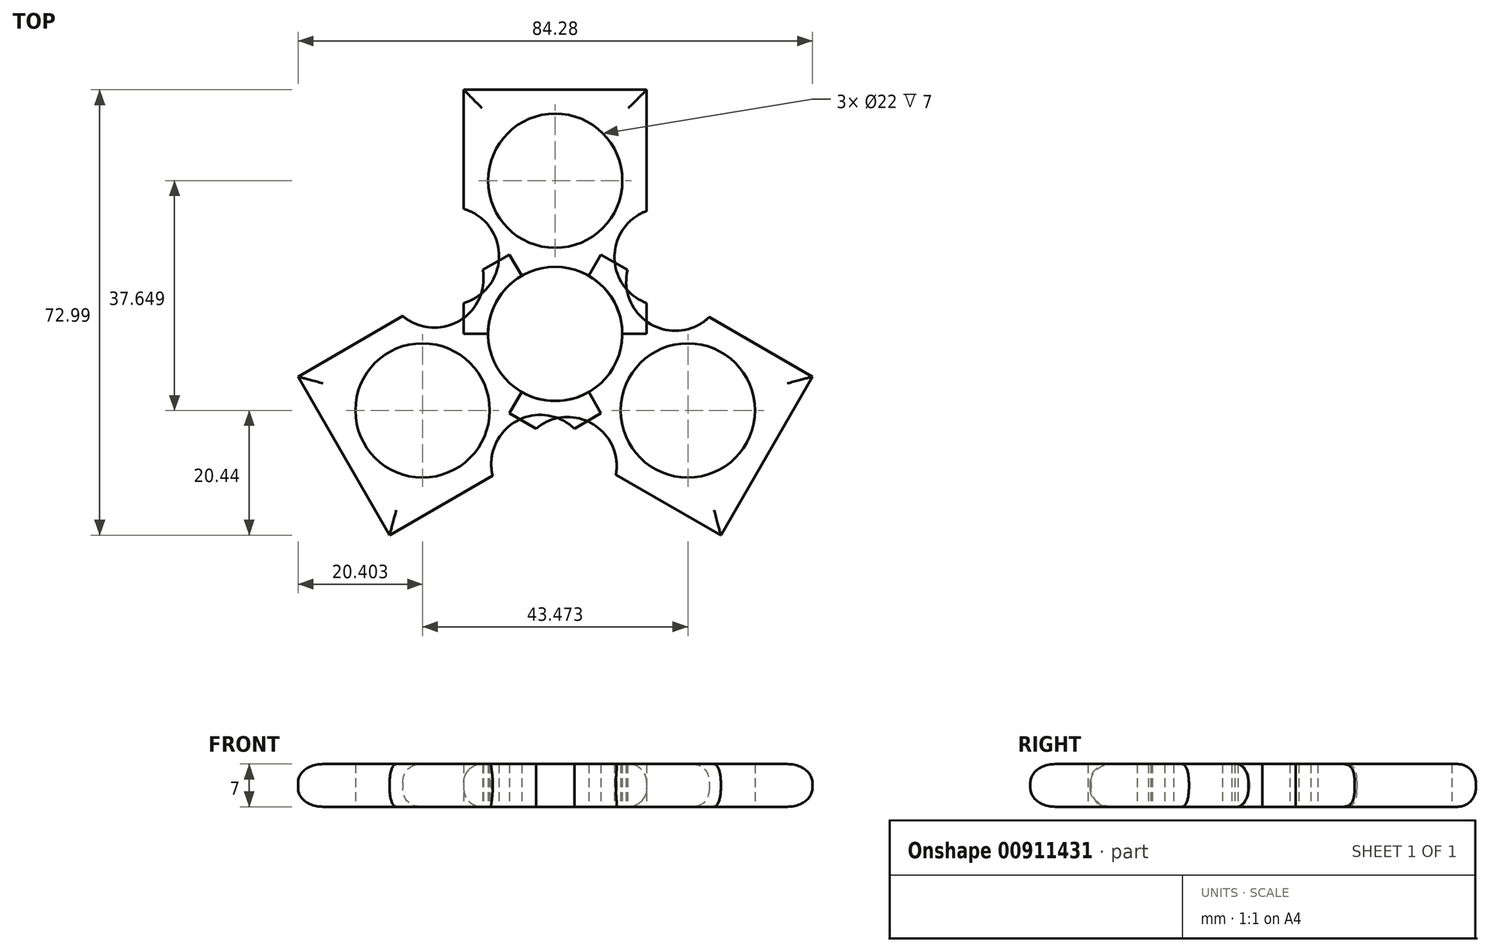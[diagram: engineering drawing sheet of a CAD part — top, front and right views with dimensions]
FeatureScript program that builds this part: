
annotation { "Feature Type Name" : "Feature", "Feature Type Description" : "" }
export const myFeature = defineFeature(function(context is Context, id is Id, definition is map)
    precondition{}
    {
        {
            var Q0;
            Q0=qCreatedBy(makeId("Top.planeOp"),FACE);
            var sketch = newSketch(context, id + "F0", { "sketchPlane" : qUnion([Q0])});
            skCircle(sketch, "E0", {"center": v(0, 0) * mm, "radius": 11 * mm});
            skLineSegment(sketch, "E1.bottom", {"start": v(0, 0) * mm, "end": v(15, 0) * mm});
            skLineSegment(sketch, "E1.top", {"start": v(0, 40) * mm, "end": v(15, 40) * mm});
            skLineSegment(sketch, "E1.left", {"start": v(0, 0) * mm, "end": v(0, 40) * mm});
            skLineSegment(sketch, "E1.right", {"start": v(15, 0) * mm, "end": v(15, 40) * mm});
            skLineSegment(sketch, "E2.bottom", {"start": v(0, 0) * mm, "end": v(-15, 0) * mm});
            skLineSegment(sketch, "E2.top", {"start": v(0, 40) * mm, "end": v(-15, 40) * mm});
            skLineSegment(sketch, "E2.right", {"start": v(-15, 0) * mm, "end": v(-15, 40) * mm});
            skLineSegment(sketch, "E3.bottom", {"start": v(-15, 0) * mm, "end": v(0, 0) * mm});
            skCircle(sketch, "E4", {"center": v(0, 25.1) * mm, "radius": 11 * mm});
            skCircle(sketch, "E5", {"center": v(17.75, 12.6) * mm, "radius": 8.04 * mm});
            skCircle(sketch, "E6", {"center": v(-17.24, 12.77) * mm, "radius": 8.04 * mm});
            skSolve(sketch);
        }
        {
            var Q0;
            {var subQ1=sQuery(id+"F0.wireOp",EDGE,"E2.top");Q0=makeQuery(id+"F0.imprint","IMPRINT",FACE,{"disambiguationData":[TD([[makeQuery(id+"F0.imprint","IMPRINT",EDGE,{"derivedFrom":subQ1}),1.0]])]});}
            var Q1;
            {var subQ6=sQuery(id+"F0.wireOp",EDGE,"E1.top");Q1=makeQuery(id+"F0.imprint","IMPRINT",FACE,{"disambiguationData":[TD([[makeQuery(id+"F0.imprint","IMPRINT",EDGE,{"derivedFrom":subQ6}),-1.0]])]});}
            extrude(context, id + "F1", {"entities" : qUnion([Q0, Q1]), "depth" : 7 * mm, "offsetDistance" : 25 * mm});
        }
        {
            var Q0;
            Q0=qCreatedBy(makeId("Front.planeOp"),FACE);
            var sketch = newSketch(context, id + "F2", { "sketchPlane" : qUnion([Q0])});
            skLineSegment(sketch, "E7", {"start": v(0, 0) * mm, "end": v(0, 54.38) * mm});
            skSolve(sketch);
        }
        {
            var Q0;
            Q0=makeQuery(id+"F1.opExtrude","SWEPT_BODY",BODY,{"disambiguationData":[OSD([sQuery(id+"F0.wireOp",EDGE,"E0"),sQuery(id+"F0.wireOp",EDGE,"E1.top"),sQuery(id+"F0.wireOp",EDGE,"E1.right"),sQuery(id+"F0.wireOp",EDGE,"E2.top"),sQuery(id+"F0.wireOp",EDGE,"E2.right"),sQuery(id+"F0.wireOp",EDGE,"E1.bottom"),sQuery(id+"F0.wireOp",EDGE,"E3.bottom"),sQuery(id+"F0.wireOp",EDGE,"E4")])]});
            var Q1;
            Q1=sQuery(id+"F2.wireOp",EDGE,"E7");
            transform(context, id + "F3", {"entities" : qUnion([Q0]), "transformType" : TransformType.ROTATION, "transformAxis" : qUnion([Q1]), "angle" : 120 * degree, "makeCopy" : true});
        }
        {
            var Q0;
            Q0=makeQuery(id+"F1.opExtrude","SWEPT_BODY",BODY,{"disambiguationData":[OSD([sQuery(id+"F0.wireOp",EDGE,"E0"),sQuery(id+"F0.wireOp",EDGE,"E1.top"),sQuery(id+"F0.wireOp",EDGE,"E1.right"),sQuery(id+"F0.wireOp",EDGE,"E2.top"),sQuery(id+"F0.wireOp",EDGE,"E2.right"),sQuery(id+"F0.wireOp",EDGE,"E1.bottom"),sQuery(id+"F0.wireOp",EDGE,"E3.bottom"),sQuery(id+"F0.wireOp",EDGE,"E4")])]});
            var Q1;
            Q1=sQuery(id+"F2.wireOp",EDGE,"E7");
            transform(context, id + "F4", {"entities" : qUnion([Q0]), "transformType" : TransformType.ROTATION, "transformAxis" : qUnion([Q1]), "angle" : 240 * degree, "makeCopy" : true});
        }
        {
            var Q0;
            Q0=makeQuery(id+"F3.opPattern","COPY",EDGE,{"derivedFrom":makeQuery(id+"F1.opExtrude","CAP_EDGE",EDGE,{"disambiguationData":[OSD([sQuery(id+"F0.wireOp",EDGE,"E1.top"),sQuery(id+"F0.wireOp",EDGE,"E2.top")])],"isStart":true}),"instanceName":"1"});
            var Q1;
            {var subQ0=sQuery(id+"F0.wireOp",EDGE,"E2.right");Q1=makeQuery(id+"F3.opPattern","COPY",EDGE,{"derivedFrom":makeQuery(id+"F1.opExtrude","CAP_EDGE",EDGE,{"disambiguationData":[OSD([subQ0]),TDD([makeQuery(id+"F0.imprint","IMPRINT",EDGE,{"disambiguationData":[TD([[makeQuery(id+"F0.imprint","INTERSECT",VERTEX,{"derivedFrom":[sQuery(id+"F0.wireOp",EDGE,"E2.top"),subQ0]}),1.0]])],"derivedFrom":subQ0})])],"isStart":true}),"instanceName":"1"});}
            var Q2;
            {var subQ0=sQuery(id+"F0.wireOp",EDGE,"E1.right");Q2=makeQuery(id+"F3.opPattern","COPY",EDGE,{"derivedFrom":makeQuery(id+"F1.opExtrude","CAP_EDGE",EDGE,{"disambiguationData":[OSD([subQ0]),TDD([makeQuery(id+"F0.imprint","IMPRINT",EDGE,{"disambiguationData":[TD([[makeQuery(id+"F0.imprint","INTERSECT",VERTEX,{"derivedFrom":[sQuery(id+"F0.wireOp",EDGE,"E1.top"),subQ0]}),1.0]])],"derivedFrom":subQ0})])],"isStart":true}),"instanceName":"1"});}
            var Q3;
            {var subQ0=sQuery(id+"F0.wireOp",EDGE,"E2.right");Q3=makeQuery(id+"F1.opExtrude","CAP_EDGE",EDGE,{"disambiguationData":[OSD([subQ0]),TDD([makeQuery(id+"F0.imprint","IMPRINT",EDGE,{"disambiguationData":[TD([[makeQuery(id+"F0.imprint","INTERSECT",VERTEX,{"derivedFrom":[sQuery(id+"F0.wireOp",EDGE,"E2.top"),subQ0]}),1.0]])],"derivedFrom":subQ0})])],"isStart":true});}
            var Q4;
            Q4=makeQuery(id+"F1.opExtrude","CAP_EDGE",EDGE,{"disambiguationData":[OSD([sQuery(id+"F0.wireOp",EDGE,"E1.top"),sQuery(id+"F0.wireOp",EDGE,"E2.top")])],"isStart":true});
            var Q5;
            {var subQ0=sQuery(id+"F0.wireOp",EDGE,"E1.right");Q5=makeQuery(id+"F1.opExtrude","CAP_EDGE",EDGE,{"disambiguationData":[OSD([subQ0]),TDD([makeQuery(id+"F0.imprint","IMPRINT",EDGE,{"disambiguationData":[TD([[makeQuery(id+"F0.imprint","INTERSECT",VERTEX,{"derivedFrom":[sQuery(id+"F0.wireOp",EDGE,"E1.top"),subQ0]}),1.0]])],"derivedFrom":subQ0})])],"isStart":true});}
            var Q6;
            {var subQ0=sQuery(id+"F0.wireOp",EDGE,"E2.right");Q6=makeQuery(id+"F4.opPattern","COPY",EDGE,{"derivedFrom":makeQuery(id+"F1.opExtrude","CAP_EDGE",EDGE,{"disambiguationData":[OSD([subQ0]),TDD([makeQuery(id+"F0.imprint","IMPRINT",EDGE,{"disambiguationData":[TD([[makeQuery(id+"F0.imprint","INTERSECT",VERTEX,{"derivedFrom":[sQuery(id+"F0.wireOp",EDGE,"E2.top"),subQ0]}),1.0]])],"derivedFrom":subQ0})])],"isStart":true}),"instanceName":"1"});}
            var Q7;
            Q7=makeQuery(id+"F4.opPattern","COPY",EDGE,{"derivedFrom":makeQuery(id+"F1.opExtrude","CAP_EDGE",EDGE,{"disambiguationData":[OSD([sQuery(id+"F0.wireOp",EDGE,"E1.top"),sQuery(id+"F0.wireOp",EDGE,"E2.top")])],"isStart":true}),"instanceName":"1"});
            var Q8;
            {var subQ0=sQuery(id+"F0.wireOp",EDGE,"E1.right");Q8=makeQuery(id+"F4.opPattern","COPY",EDGE,{"derivedFrom":makeQuery(id+"F1.opExtrude","CAP_EDGE",EDGE,{"disambiguationData":[OSD([subQ0]),TDD([makeQuery(id+"F0.imprint","IMPRINT",EDGE,{"disambiguationData":[TD([[makeQuery(id+"F0.imprint","INTERSECT",VERTEX,{"derivedFrom":[sQuery(id+"F0.wireOp",EDGE,"E1.top"),subQ0]}),1.0]])],"derivedFrom":subQ0})])],"isStart":true}),"instanceName":"1"});}
            fillet(context, id + "F5", {"entities" : qUnion([Q0, Q1, Q2, Q3, Q4, Q5, Q6, Q7, Q8]), "radius" : 3 * mm, "tangentPropagation" : true, "allowEdgeOverflow" : false});
        }
        {
            var Q0;
            Q0=makeQuery(id+"F4.opPattern","COPY",EDGE,{"derivedFrom":makeQuery(id+"F1.opExtrude","CAP_EDGE",EDGE,{"disambiguationData":[OSD([sQuery(id+"F0.wireOp",EDGE,"E1.top"),sQuery(id+"F0.wireOp",EDGE,"E2.top")])],"isStart":false}),"instanceName":"1"});
            var Q1;
            {var subQ0=sQuery(id+"F0.wireOp",EDGE,"E2.right");Q1=makeQuery(id+"F4.opPattern","COPY",EDGE,{"derivedFrom":makeQuery(id+"F1.opExtrude","CAP_EDGE",EDGE,{"disambiguationData":[OSD([subQ0]),TDD([makeQuery(id+"F0.imprint","IMPRINT",EDGE,{"disambiguationData":[TD([[makeQuery(id+"F0.imprint","INTERSECT",VERTEX,{"derivedFrom":[sQuery(id+"F0.wireOp",EDGE,"E2.top"),subQ0]}),1.0]])],"derivedFrom":subQ0})])],"isStart":false}),"instanceName":"1"});}
            var Q2;
            {var subQ0=sQuery(id+"F0.wireOp",EDGE,"E1.right");Q2=makeQuery(id+"F4.opPattern","COPY",EDGE,{"derivedFrom":makeQuery(id+"F1.opExtrude","CAP_EDGE",EDGE,{"disambiguationData":[OSD([subQ0]),TDD([makeQuery(id+"F0.imprint","IMPRINT",EDGE,{"disambiguationData":[TD([[makeQuery(id+"F0.imprint","INTERSECT",VERTEX,{"derivedFrom":[sQuery(id+"F0.wireOp",EDGE,"E1.top"),subQ0]}),1.0]])],"derivedFrom":subQ0})])],"isStart":false}),"instanceName":"1"});}
            var Q3;
            {var subQ0=sQuery(id+"F0.wireOp",EDGE,"E2.right");Q3=makeQuery(id+"F3.opPattern","COPY",EDGE,{"derivedFrom":makeQuery(id+"F1.opExtrude","CAP_EDGE",EDGE,{"disambiguationData":[OSD([subQ0]),TDD([makeQuery(id+"F0.imprint","IMPRINT",EDGE,{"disambiguationData":[TD([[makeQuery(id+"F0.imprint","INTERSECT",VERTEX,{"derivedFrom":[sQuery(id+"F0.wireOp",EDGE,"E2.top"),subQ0]}),1.0]])],"derivedFrom":subQ0})])],"isStart":false}),"instanceName":"1"});}
            var Q4;
            Q4=makeQuery(id+"F3.opPattern","COPY",EDGE,{"derivedFrom":makeQuery(id+"F1.opExtrude","CAP_EDGE",EDGE,{"disambiguationData":[OSD([sQuery(id+"F0.wireOp",EDGE,"E1.top"),sQuery(id+"F0.wireOp",EDGE,"E2.top")])],"isStart":false}),"instanceName":"1"});
            var Q5;
            {var subQ0=sQuery(id+"F0.wireOp",EDGE,"E1.right");Q5=makeQuery(id+"F3.opPattern","COPY",EDGE,{"derivedFrom":makeQuery(id+"F1.opExtrude","CAP_EDGE",EDGE,{"disambiguationData":[OSD([subQ0]),TDD([makeQuery(id+"F0.imprint","IMPRINT",EDGE,{"disambiguationData":[TD([[makeQuery(id+"F0.imprint","INTERSECT",VERTEX,{"derivedFrom":[sQuery(id+"F0.wireOp",EDGE,"E1.top"),subQ0]}),1.0]])],"derivedFrom":subQ0})])],"isStart":false}),"instanceName":"1"});}
            var Q6;
            {var subQ0=sQuery(id+"F0.wireOp",EDGE,"E2.right");var subQ1=makeQuery(id+"F0.imprint","IMPRINT",EDGE,{"disambiguationData":[TD([[makeQuery(id+"F0.imprint","INTERSECT",VERTEX,{"derivedFrom":[sQuery(id+"F0.wireOp",EDGE,"E2.top"),subQ0]}),1.0]])],"derivedFrom":subQ0});Q6=makeQuery(id+"F5.opFillet","BLEND_EDGE",EDGE,{"blendedFrom":[makeQuery(id+"F1.opExtrude","CAP_EDGE",EDGE,{"disambiguationData":[OSD([subQ0]),TDD([subQ1])],"isStart":true}),makeQuery(id+"F1.opExtrude","SWEPT_FACE",FACE,{"disambiguationData":[OSD([subQ0]),TDD([subQ1])]})],"blendedInto":[makeQuery(id+"F1.opExtrude","SWEPT_FACE",FACE,{"disambiguationData":[OSD([subQ0]),TDD([subQ1])]})]});}
            var Q7;
            Q7=makeQuery(id+"F1.opExtrude","CAP_EDGE",EDGE,{"disambiguationData":[OSD([sQuery(id+"F0.wireOp",EDGE,"E1.top"),sQuery(id+"F0.wireOp",EDGE,"E2.top")])],"isStart":false});
            var Q8;
            {var subQ0=sQuery(id+"F0.wireOp",EDGE,"E2.right");Q8=makeQuery(id+"F1.opExtrude","CAP_EDGE",EDGE,{"disambiguationData":[OSD([subQ0]),TDD([makeQuery(id+"F0.imprint","IMPRINT",EDGE,{"disambiguationData":[TD([[makeQuery(id+"F0.imprint","INTERSECT",VERTEX,{"derivedFrom":[sQuery(id+"F0.wireOp",EDGE,"E2.top"),subQ0]}),1.0]])],"derivedFrom":subQ0})])],"isStart":false});}
            var Q9;
            {var subQ0=sQuery(id+"F0.wireOp",EDGE,"E1.right");Q9=makeQuery(id+"F1.opExtrude","CAP_EDGE",EDGE,{"disambiguationData":[OSD([subQ0]),TDD([makeQuery(id+"F0.imprint","IMPRINT",EDGE,{"disambiguationData":[TD([[makeQuery(id+"F0.imprint","INTERSECT",VERTEX,{"derivedFrom":[sQuery(id+"F0.wireOp",EDGE,"E1.top"),subQ0]}),1.0]])],"derivedFrom":subQ0})])],"isStart":false});}
            fillet(context, id + "F6", {"entities" : qUnion([Q0, Q1, Q2, Q3, Q4, Q5, Q6, Q7, Q8, Q9]), "radius" : 3 * mm, "tangentPropagation" : true, "allowEdgeOverflow" : false});
        }
    });
